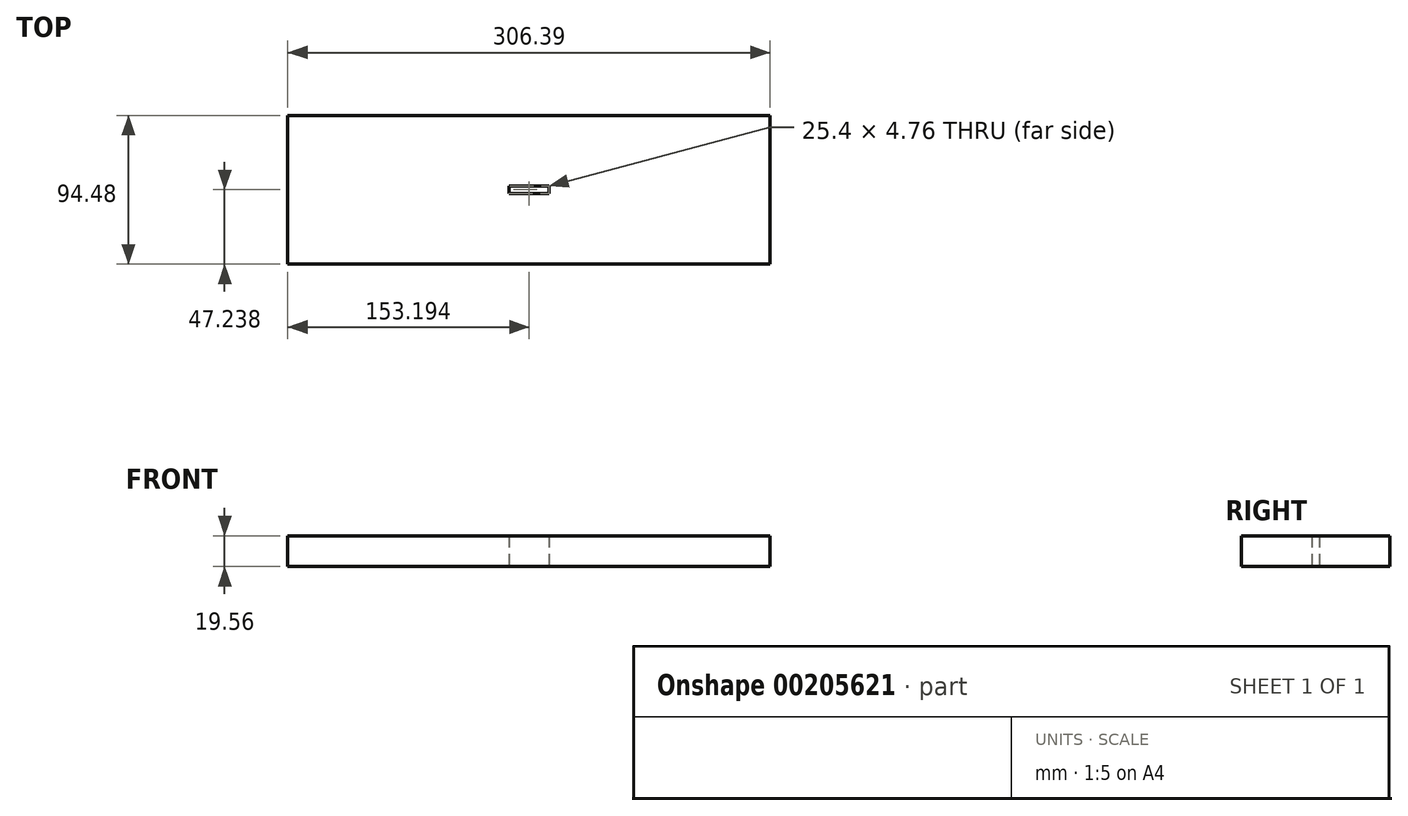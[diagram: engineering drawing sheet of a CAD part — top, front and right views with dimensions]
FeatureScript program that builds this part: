
annotation { "Feature Type Name" : "Feature", "Feature Type Description" : "" }
export const myFeature = defineFeature(function(context is Context, id is Id, definition is map)
    precondition{}
    {
        {
            var Q0;
            Q0=qCreatedBy(makeId("Top.planeOp"),FACE);
            var sketch = newSketch(context, id + "F0", { "sketchPlane" : qUnion([Q0])});
            skLineSegment(sketch, "E0", {"start": v(0, 0) * mm, "end": v(91.65, 0) * mm});
            skLineSegment(sketch, "E1", {"start": v(0, 0) * mm, "end": v(306.39, 0) * mm});
            skPoint(sketch, "E1.endSnap0", {"position": v(45.83, 0) * mm});
            skPoint(sketch, "E2.endSnap0", {"position": v(153.2, 0) * mm});
            skLineSegment(sketch, "E3", {"start": v(0, -94.48) * mm, "end": v(0, 0) * mm});
            skLineSegment(sketch, "E4", {"start": v(306.39, 0) * mm, "end": v(306.39, -94.48) * mm});
            skLineSegment(sketch, "E5", {"start": v(306.39, -94.48) * mm, "end": v(0, -94.48) * mm});
            skLineSegment(sketch, "E6", {"start": v(153.2, -49.62) * mm, "end": v(140.5, -49.62) * mm});
            skLineSegment(sketch, "E7.MirrorCS", {"start": v(153.2, -44.86) * mm, "end": v(140.5, -44.86) * mm});
            skLineSegment(sketch, "E8", {"start": v(140.5, -49.62) * mm, "end": v(140.5, -44.86) * mm});
            skLineSegment(sketch, "E9.MirrorCS", {"start": v(153.2, -44.86) * mm, "end": v(165.9, -44.86) * mm});
            skLineSegment(sketch, "E10.MirrorCS", {"start": v(153.2, -49.62) * mm, "end": v(165.9, -49.62) * mm});
            skLineSegment(sketch, "E11.MirrorCS", {"start": v(165.9, -49.62) * mm, "end": v(165.9, -44.86) * mm});
            skSolve(sketch);
        }
        {
            var Q0;
            {var subQ1=sQuery(id+"F0.wireOp",EDGE,"E3");Q0=makeQuery(id+"F0.imprint","IMPRINT",FACE,{"disambiguationData":[TD([[makeQuery(id+"F0.imprint","IMPRINT",EDGE,{"derivedFrom":subQ1}),-1.0]])]});}
            extrude(context, id + "F1", {"entities" : qUnion([Q0]), "depth" : 19.56 * mm});
        }
    });
